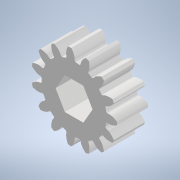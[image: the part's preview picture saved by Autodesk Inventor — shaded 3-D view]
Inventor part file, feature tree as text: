
AUTODESK INVENTOR PART (.ipt)
format: ipt  version: 2022 (Build 260153000, 153)  size: 2,962,432 bytes
history: native  units: mm
features: sketch x2, extrude x2
ambient origin geometry x8: Origin, YZ Plane, XZ Plane, XY Plane, X Axis, Y Axis, Z Axis, Center Point
bodies: Solid1 (feature_tree)
feature tree (4):
  sketch  "Sketch1"  dims[d2=6.2mm d3=0.0mm d34=3.1mm]
  extrude  "Extrusion2"  Depth=6.2mm
  extrude  "Extrusion7"  Depth=10.0mm
  sketch  "Sketch6"  dims[d35=60.0mm d37=360.0deg d39=0.5mm d40=10.0mm d41=0.0mm]
